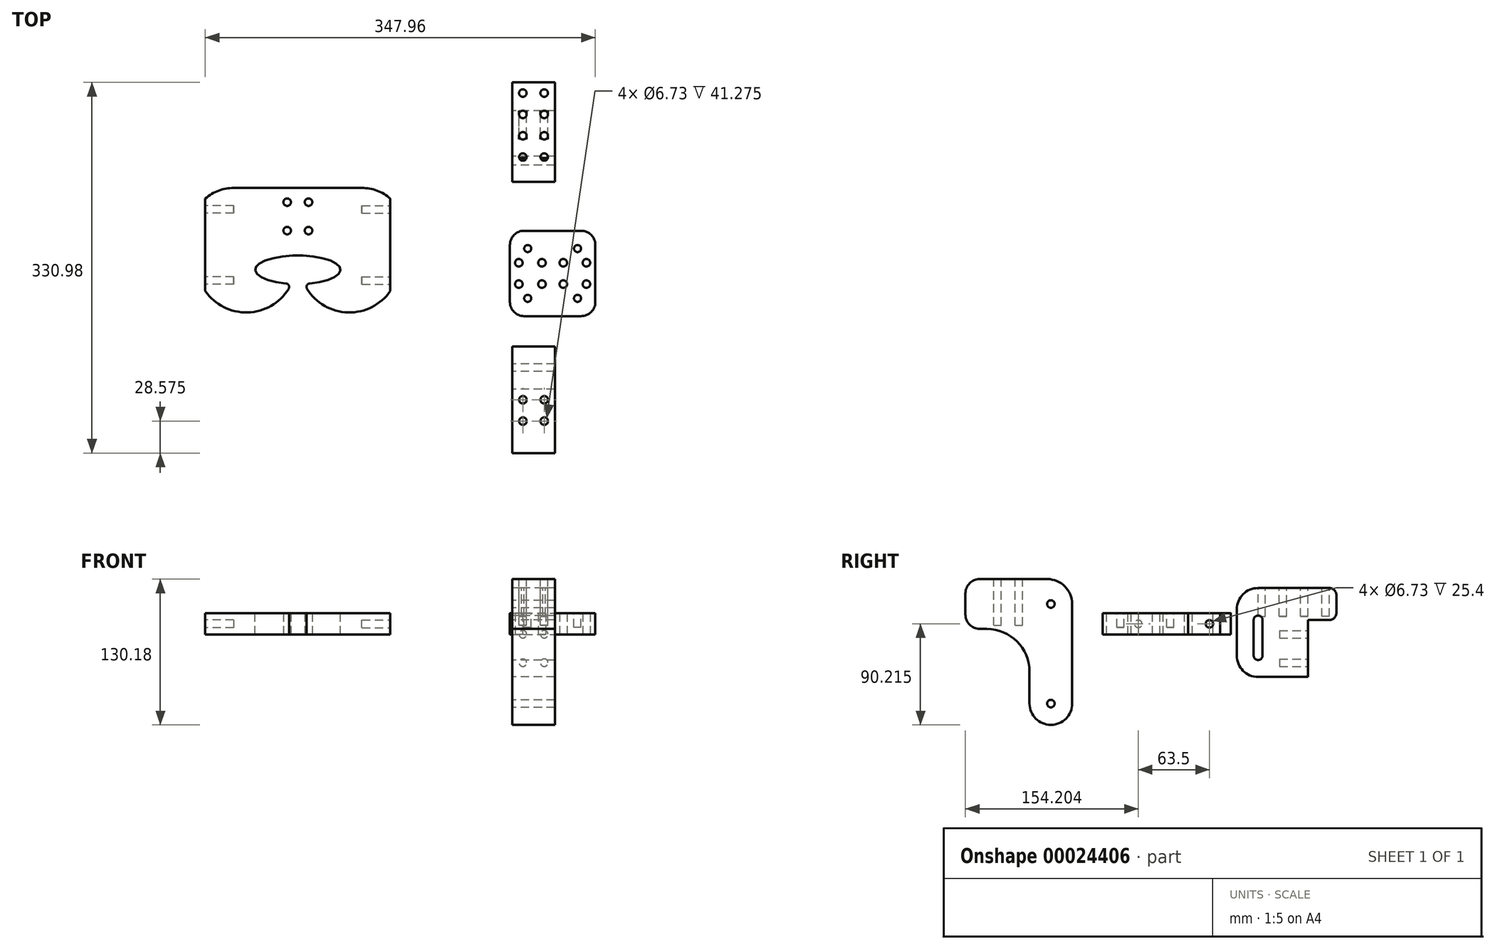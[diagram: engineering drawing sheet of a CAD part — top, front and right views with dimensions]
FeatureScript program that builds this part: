
annotation { "Feature Type Name" : "Feature", "Feature Type Description" : "" }
export const myFeature = defineFeature(function(context is Context, id is Id, definition is map)
    precondition{}
    {
        {
            var Q0;
            Q0=qCreatedBy(makeId("Top.planeOp"),FACE);
            var sketch = newSketch(context, id + "F0", { "sketchPlane" : qUnion([Q0])});
            skLineSegment(sketch, "E0.bottom", {"start": v(10.68, 0) * mm, "end": v(61.48, 0) * mm});
            skLineSegment(sketch, "E0.top", {"start": v(10.68, 76.2) * mm, "end": v(61.48, 76.2) * mm});
            skLineSegment(sketch, "E0.left", {"start": v(-2.02, 12.7) * mm, "end": v(-2.02, 63.5) * mm});
            skLineSegment(sketch, "E0.right", {"start": v(74.18, 12.7) * mm, "end": v(74.18, 63.5) * mm});
            skPoint(sketch, "E1.visualSharp", {"position": v(-2.02, 76.2) * mm});
            skArc(sketch, "E1.filletArc", {"start": v(10.68, 76.2) * mm, "mid": v(1.7, 72.48) * mm, "end": v(-2.02, 63.5) * mm});
            skPoint(sketch, "E2.visualSharp", {"position": v(74.18, 76.2) * mm});
            skArc(sketch, "E2.filletArc", {"start": v(74.18, 63.5) * mm, "mid": v(70.46, 72.48) * mm, "end": v(61.48, 76.2) * mm});
            skPoint(sketch, "E3.visualSharp", {"position": v(74.18, 0) * mm});
            skArc(sketch, "E3.filletArc", {"start": v(61.48, 0) * mm, "mid": v(70.46, 3.72) * mm, "end": v(74.18, 12.7) * mm});
            skPoint(sketch, "E4.visualSharp", {"position": v(-2.02, 0) * mm});
            skArc(sketch, "E4.filletArc", {"start": v(-2.02, 12.7) * mm, "mid": v(1.7, 3.72) * mm, "end": v(10.68, 0) * mm});
            skCircle(sketch, "E5", {"center": v(26.56, 28.57) * mm, "radius": 3.37 * mm});
            skCircle(sketch, "E6", {"center": v(26.56, 47.62) * mm, "radius": 3.37 * mm});
            skCircle(sketch, "E7", {"center": v(45.6, 47.62) * mm, "radius": 3.37 * mm});
            skCircle(sketch, "E8", {"center": v(45.6, 28.57) * mm, "radius": 3.37 * mm});
            skLineSegment(sketch, "E9", {"start": v(26.56, 47.62) * mm, "end": v(45.6, 47.62) * mm, "construction": true});
            skLineSegment(sketch, "E10", {"start": v(45.6, 28.58) * mm, "end": v(26.56, 28.58) * mm, "construction": true});
            skLineSegment(sketch, "E11", {"start": v(26.56, 47.62) * mm, "end": v(26.56, 28.57) * mm, "construction": true});
            skLineSegment(sketch, "E12", {"start": v(45.6, 47.62) * mm, "end": v(45.6, 28.57) * mm, "construction": true});
            skLineSegment(sketch, "E13", {"start": v(36.08, 28.58) * mm, "end": v(36.08, 0) * mm, "construction": true});
            skLineSegment(sketch, "E14", {"start": v(26.56, 38.1) * mm, "end": v(-2.02, 38.1) * mm, "construction": true});
            skLineSegment(sketch, "E15", {"start": v(45.6, 47.62) * mm, "end": v(74.18, 47.63) * mm, "construction": true});
            skLineSegment(sketch, "E16", {"start": v(26.56, 47.62) * mm, "end": v(-2.02, 47.62) * mm, "construction": true});
            skLineSegment(sketch, "E17", {"start": v(26.56, 28.57) * mm, "end": v(-2.02, 28.57) * mm, "construction": true});
            skLineSegment(sketch, "E18", {"start": v(45.6, 28.57) * mm, "end": v(74.18, 28.57) * mm, "construction": true});
            skCircle(sketch, "E19", {"center": v(66.23, 28.58) * mm, "radius": 3.37 * mm});
            skCircle(sketch, "E20", {"center": v(66.23, 47.63) * mm, "radius": 3.37 * mm});
            skCircle(sketch, "E21", {"center": v(5.93, 47.62) * mm, "radius": 3.37 * mm});
            skCircle(sketch, "E22", {"center": v(5.93, 28.57) * mm, "radius": 3.37 * mm});
            skSolve(sketch);
        }
        {
            var Q0;
            Q0 = qSketchRegion(id + "F0", true);
            extrude(context, id + "F1", {"entities" : qUnion([Q0]), "depth" : 19.05 * mm});
        }
        {
            var Q0;
            Q0=makeQuery(id+"F1.opExtrude","CAP_FACE",FACE,{"disambiguationData":[OSD([sQuery(id+"F0.wireOp",EDGE,"E0.bottom"),sQuery(id+"F0.wireOp",EDGE,"E0.top"),sQuery(id+"F0.wireOp",EDGE,"E0.left"),sQuery(id+"F0.wireOp",EDGE,"E0.right"),sQuery(id+"F0.wireOp",EDGE,"E1.filletArc"),sQuery(id+"F0.wireOp",EDGE,"E2.filletArc"),sQuery(id+"F0.wireOp",EDGE,"E3.filletArc"),sQuery(id+"F0.wireOp",EDGE,"E4.filletArc"),sQuery(id+"F0.wireOp",EDGE,"E5"),sQuery(id+"F0.wireOp",EDGE,"E6"),sQuery(id+"F0.wireOp",EDGE,"E7"),sQuery(id+"F0.wireOp",EDGE,"E8")])],"isStart":false});
            var sketch = newSketch(context, id + "F2", { "sketchPlane" : qUnion([Q0])});
            skCircle(sketch, "E23", {"center": v(13.86, 60.33) * mm, "radius": 3.18 * mm});
            skCircle(sketch, "E24", {"center": v(58.3, 60.33) * mm, "radius": 3.18 * mm});
            skCircle(sketch, "E25", {"center": v(58.3, 15.88) * mm, "radius": 3.18 * mm});
            skCircle(sketch, "E26", {"center": v(13.86, 15.88) * mm, "radius": 3.18 * mm});
            skLineSegment(sketch, "E27", {"start": v(13.86, 60.33) * mm, "end": v(58.3, 60.33) * mm, "construction": true});
            skLineSegment(sketch, "E28", {"start": v(58.3, 60.33) * mm, "end": v(58.3, 15.88) * mm, "construction": true});
            skLineSegment(sketch, "E29", {"start": v(58.3, 15.88) * mm, "end": v(13.86, 15.88) * mm, "construction": true});
            skLineSegment(sketch, "E30", {"start": v(13.86, 15.88) * mm, "end": v(13.86, 60.33) * mm, "construction": true});
            skLineSegment(sketch, "E31", {"start": v(36.08, 0) * mm, "end": v(36.08, 15.88) * mm, "construction": true});
            skLineSegment(sketch, "E32", {"start": v(13.86, 38.1) * mm, "end": v(-2.02, 38.1) * mm, "construction": true});
            skSolve(sketch);
        }
        {
            var Q0;
            Q0=makeQuery(id+"F2.imprint","IMPRINT",FACE,{"disambiguationData":[TD([[makeQuery(id+"F2.imprint","IMPRINT",EDGE,{"derivedFrom":sQuery(id+"F2.wireOp",EDGE,"E23")}),1.0]])]});
            var Q1;
            Q1=makeQuery(id+"F2.imprint","IMPRINT",FACE,{"disambiguationData":[TD([[makeQuery(id+"F2.imprint","IMPRINT",EDGE,{"derivedFrom":sQuery(id+"F2.wireOp",EDGE,"E24")}),1.0]])]});
            var Q2;
            Q2=makeQuery(id+"F2.imprint","IMPRINT",FACE,{"disambiguationData":[TD([[makeQuery(id+"F2.imprint","IMPRINT",EDGE,{"derivedFrom":sQuery(id+"F2.wireOp",EDGE,"E25")}),1.0]])]});
            var Q3;
            Q3=makeQuery(id+"F2.imprint","IMPRINT",FACE,{"disambiguationData":[TD([[makeQuery(id+"F2.imprint","IMPRINT",EDGE,{"derivedFrom":sQuery(id+"F2.wireOp",EDGE,"E26")}),1.0]])]});
            var Q4;
            Q4=sQuery(id+"F2.wireOp",EDGE,"E23");
            var Q5;
            Q5=sQuery(id+"F2.wireOp",EDGE,"E26");
            var Q6;
            Q6=sQuery(id+"F2.wireOp",EDGE,"E25");
            var Q7;
            Q7=sQuery(id+"F2.wireOp",EDGE,"E24");
            extrude(context, id + "F3", {"entities" : qUnion([Q0, Q1, Q2, Q3]), "operationType" : NewBodyOperationType.REMOVE, "surfaceEntities" : qUnion([Q4, Q5, Q6, Q7]), "oppositeDirection" : true, "depth" : 12.7 * mm});
        }
        {
            var Q0;
            Q0=qCreatedBy(makeId("Right.planeOp"),FACE);
            var sketch = newSketch(context, id + "F4", { "sketchPlane" : qUnion([Q0])});
            skLineSegment(sketch, "E33.bottom", {"start": v(-49.27, 49.49) * mm, "end": v(-109.6, 49.49) * mm});
            skLineSegment(sketch, "E33.top", {"start": v(-46.1, -80.69) * mm, "end": v(-46.1, -80.69) * mm});
            skLineSegment(sketch, "E33.left", {"start": v(-27.04, 27.26) * mm, "end": v(-27.04, -61.64) * mm});
            skLineSegment(sketch, "E33.right", {"start": v(-122.3, 36.79) * mm, "end": v(-122.3, 17.74) * mm});
            skLineSegment(sketch, "E34", {"start": v(-65.14, -61.64) * mm, "end": v(-65.14, -33.06) * mm});
            skLineSegment(sketch, "E35", {"start": v(-103.24, 5.04) * mm, "end": v(-109.6, 5.04) * mm});
            skPoint(sketch, "E36.visualSharp", {"position": v(-27.04, 49.49) * mm});
            skArc(sketch, "E36.filletArc", {"start": v(-27.04, 27.26) * mm, "mid": v(-33.55, 42.98) * mm, "end": v(-49.27, 49.49) * mm});
            skPoint(sketch, "E37.visualSharp", {"position": v(-122.3, 49.49) * mm});
            skArc(sketch, "E37.filletArc", {"start": v(-109.6, 49.49) * mm, "mid": v(-118.57, 45.77) * mm, "end": v(-122.3, 36.79) * mm});
            skPoint(sketch, "E38.visualSharp", {"position": v(-122.3, 5.04) * mm});
            skArc(sketch, "E38.filletArc", {"start": v(-122.3, 17.74) * mm, "mid": v(-118.57, 8.76) * mm, "end": v(-109.6, 5.04) * mm});
            skPoint(sketch, "E39.visualSharp", {"position": v(-65.14, -80.69) * mm});
            skArc(sketch, "E39.filletArc", {"start": v(-65.14, -61.64) * mm, "mid": v(-59.56, -75.1) * mm, "end": v(-46.1, -80.69) * mm});
            skPoint(sketch, "E40.visualSharp", {"position": v(-27.04, -80.69) * mm});
            skArc(sketch, "E40.filletArc", {"start": v(-46.1, -80.69) * mm, "mid": v(-32.62, -75.1) * mm, "end": v(-27.04, -61.64) * mm});
            skPoint(sketch, "E41.visualSharp", {"position": v(-65.14, 5.04) * mm});
            skArc(sketch, "E41.filletArc", {"start": v(-65.14, -33.06) * mm, "mid": v(-76.3, -6.12) * mm, "end": v(-103.24, 5.04) * mm});
            skCircle(sketch, "E42", {"center": v(-46.1, 27.26) * mm, "radius": 3.37 * mm});
            skCircle(sketch, "E43", {"center": v(-46.1, -61.64) * mm, "radius": 3.37 * mm});
            skSolve(sketch);
        }
        {
            var Q0;
            Q0=makeQuery(id+"F4.imprint","IMPRINT",FACE,{"disambiguationData":[TD([[makeQuery(id+"F4.imprint","IMPRINT",EDGE,{"derivedFrom":sQuery(id+"F4.wireOp",EDGE,"E33.bottom")}),1.0]])]});
            extrude(context, id + "F5", {"entities" : qUnion([Q0]), "depth" : 38.1 * mm});
        }
        {
            var Q0;
            Q0=makeQuery(id+"F5.opExtrude","SWEPT_FACE",FACE,{"disambiguationData":[OSD([sQuery(id+"F4.wireOp",EDGE,"E33.bottom")])]});
            var sketch = newSketch(context, id + "F6", { "sketchPlane" : qUnion([Q0])});
            skLineSegment(sketch, "E44", {"start": v(19.05, -49.27) * mm, "end": v(19.05, -109.6) * mm, "construction": true});
            skCircle(sketch, "E45", {"center": v(28.58, -93.72) * mm, "radius": 3.37 * mm});
            skCircle(sketch, "E46", {"center": v(28.58, -74.67) * mm, "radius": 3.37 * mm});
            skCircle(sketch, "E47", {"center": v(9.53, -74.67) * mm, "radius": 3.37 * mm});
            skCircle(sketch, "E48", {"center": v(9.53, -93.72) * mm, "radius": 3.37 * mm});
            skLineSegment(sketch, "E49", {"start": v(9.53, -74.67) * mm, "end": v(19.05, -74.67) * mm, "construction": true});
            skLineSegment(sketch, "E50", {"start": v(28.58, -93.72) * mm, "end": v(28.58, -74.67) * mm, "construction": true});
            skLineSegment(sketch, "E51", {"start": v(9.53, -93.72) * mm, "end": v(28.58, -93.72) * mm, "construction": true});
            skLineSegment(sketch, "E52", {"start": v(9.53, -93.72) * mm, "end": v(9.53, -74.67) * mm, "construction": true});
            skLineSegment(sketch, "E53", {"start": v(19.05, -74.67) * mm, "end": v(28.58, -74.67) * mm, "construction": true});
            skSolve(sketch);
        }
        {
            var Q0;
            Q0=makeQuery(id+"F6.imprint","IMPRINT",FACE,{"disambiguationData":[TD([[makeQuery(id+"F6.imprint","IMPRINT",EDGE,{"derivedFrom":sQuery(id+"F6.wireOp",EDGE,"E47")}),1.0]])]});
            var Q1;
            Q1=makeQuery(id+"F6.imprint","IMPRINT",FACE,{"disambiguationData":[TD([[makeQuery(id+"F6.imprint","IMPRINT",EDGE,{"derivedFrom":sQuery(id+"F6.wireOp",EDGE,"E46")}),1.0]])]});
            var Q2;
            Q2=makeQuery(id+"F6.imprint","IMPRINT",FACE,{"disambiguationData":[TD([[makeQuery(id+"F6.imprint","IMPRINT",EDGE,{"derivedFrom":sQuery(id+"F6.wireOp",EDGE,"E45")}),1.0]])]});
            var Q3;
            Q3=makeQuery(id+"F6.imprint","IMPRINT",FACE,{"disambiguationData":[TD([[makeQuery(id+"F6.imprint","IMPRINT",EDGE,{"derivedFrom":sQuery(id+"F6.wireOp",EDGE,"E48")}),1.0]])]});
            extrude(context, id + "F7", {"entities" : qUnion([Q0, Q1, Q2, Q3]), "operationType" : NewBodyOperationType.REMOVE, "oppositeDirection" : true, "depth" : 41.27 * mm});
        }
        {
            var Q0;
            Q0=qCreatedBy(makeId("Right.planeOp"),FACE);
            var sketch = newSketch(context, id + "F8", { "sketchPlane" : qUnion([Q0])});
            skLineSegment(sketch, "E54.bottom", {"start": v(138.84, -37.85) * mm, "end": v(183.29, -37.85) * mm});
            skLineSegment(sketch, "E54.top", {"start": v(138.84, 41.52) * mm, "end": v(202.34, 41.52) * mm});
            skLineSegment(sketch, "E54.left", {"start": v(119.79, -18.8) * mm, "end": v(119.79, 22.47) * mm});
            skLineSegment(sketch, "E54.right", {"start": v(208.69, -37.85) * mm, "end": v(208.69, 12.95) * mm, "construction": true});
            skLineSegment(sketch, "E55", {"start": v(183.29, -37.85) * mm, "end": v(183.29, -37.85) * mm});
            skLineSegment(sketch, "E56", {"start": v(183.29, 12.95) * mm, "end": v(202.34, 12.95) * mm});
            skLineSegment(sketch, "E57", {"start": v(183.29, -37.85) * mm, "end": v(183.29, 12.95) * mm});
            skLineSegment(sketch, "E58", {"start": v(208.69, 19.3) * mm, "end": v(208.69, 35.17) * mm});
            skLineSegment(sketch, "E59", {"start": v(183.29, -37.85) * mm, "end": v(208.69, -37.85) * mm, "construction": true});
            skPoint(sketch, "E60.visualSharp", {"position": v(119.79, 41.52) * mm});
            skArc(sketch, "E60.filletArc", {"start": v(138.84, 41.52) * mm, "mid": v(125.37, 35.94) * mm, "end": v(119.79, 22.47) * mm});
            skPoint(sketch, "E61.visualSharp", {"position": v(119.79, -37.85) * mm});
            skArc(sketch, "E61.filletArc", {"start": v(119.79, -18.8) * mm, "mid": v(125.37, -32.27) * mm, "end": v(138.84, -37.85) * mm});
            skPoint(sketch, "E62.visualSharp", {"position": v(208.69, 41.52) * mm});
            skArc(sketch, "E62.filletArc", {"start": v(208.69, 35.17) * mm, "mid": v(206.83, 39.66) * mm, "end": v(202.34, 41.52) * mm});
            skPoint(sketch, "E63.visualSharp", {"position": v(208.69, 12.95) * mm});
            skArc(sketch, "E63.filletArc", {"start": v(202.34, 12.95) * mm, "mid": v(206.83, 14.8) * mm, "end": v(208.69, 19.3) * mm});
            skArc(sketch, "E64", {"start": v(134.86, -18.8) * mm, "mid": v(138.84, -22.78) * mm, "end": v(142.81, -18.8) * mm});
            skArc(sketch, "E65", {"start": v(142.81, 12.95) * mm, "mid": v(138.84, 16.92) * mm, "end": v(134.86, 12.95) * mm});
            skLineSegment(sketch, "E66", {"start": v(142.81, 12.95) * mm, "end": v(142.81, -18.8) * mm});
            skLineSegment(sketch, "E67", {"start": v(134.86, 12.95) * mm, "end": v(134.86, -18.8) * mm});
            skSolve(sketch);
        }
        {
            var Q0;
            Q0 = qSketchRegion(id + "F8", true);
            extrude(context, id + "F9", {"entities" : qUnion([Q0]), "depth" : 38.1 * mm});
        }
        {
            var Q0;
            Q0=makeQuery(id+"F9.opExtrude","SWEPT_FACE",FACE,{"disambiguationData":[OSD([sQuery(id+"F8.wireOp",EDGE,"E54.top")])]});
            var sketch = newSketch(context, id + "F10", { "sketchPlane" : qUnion([Q0])});
            skCircle(sketch, "E68", {"center": v(28.58, 199.16) * mm, "radius": 3.37 * mm});
            skCircle(sketch, "E69", {"center": v(28.58, 180.11) * mm, "radius": 3.37 * mm});
            skCircle(sketch, "E70", {"center": v(28.58, 161.06) * mm, "radius": 3.37 * mm});
            skCircle(sketch, "E71", {"center": v(28.58, 142.01) * mm, "radius": 3.37 * mm});
            skCircle(sketch, "E72", {"center": v(9.53, 142.01) * mm, "radius": 3.37 * mm});
            skCircle(sketch, "E73", {"center": v(9.53, 161.06) * mm, "radius": 3.37 * mm});
            skCircle(sketch, "E74", {"center": v(9.53, 180.11) * mm, "radius": 3.37 * mm});
            skCircle(sketch, "E75", {"center": v(9.53, 199.16) * mm, "radius": 3.37 * mm});
            skSolve(sketch);
        }
        {
            var Q0;
            {var subQ0=makeQuery(id+"F9.opExtrude","SWEPT_EDGE",EDGE,{"disambiguationData":[OSD([sQuery(id+"F8.wireOp",EDGE,"E54.top"),sQuery(id+"F8.wireOp",EDGE,"E62.filletArc")])]});var subQ1=sQuery(id+"F10.wireOp",EDGE,"E75");var subQ3=makeQuery(id+"F10.imprint","INTERSECT",VERTEX,{"disambiguationData":[OD(0.0)],"derivedFrom":[subQ0,subQ1]});Q0=makeQuery(id+"F10.imprint","IMPRINT",FACE,{"disambiguationData":[TD([[makeQuery(id+"F10.imprint","IMPRINT",EDGE,{"disambiguationData":[TD([[subQ3,-1.0]])],"derivedFrom":subQ1}),1.0]])]});}
            var Q1;
            Q1=makeQuery(id+"F10.imprint","IMPRINT",FACE,{"disambiguationData":[TD([[makeQuery(id+"F10.imprint","IMPRINT",EDGE,{"derivedFrom":sQuery(id+"F10.wireOp",EDGE,"E69")}),1.0]])]});
            var Q2;
            Q2=makeQuery(id+"F10.imprint","IMPRINT",FACE,{"disambiguationData":[TD([[makeQuery(id+"F10.imprint","IMPRINT",EDGE,{"derivedFrom":sQuery(id+"F10.wireOp",EDGE,"E74")}),1.0]])]});
            var Q3;
            Q3=makeQuery(id+"F10.imprint","IMPRINT",FACE,{"disambiguationData":[TD([[makeQuery(id+"F10.imprint","IMPRINT",EDGE,{"derivedFrom":sQuery(id+"F10.wireOp",EDGE,"E70")}),1.0]])]});
            var Q4;
            {var subQ0=makeQuery(id+"F9.opExtrude","SWEPT_EDGE",EDGE,{"disambiguationData":[OSD([sQuery(id+"F8.wireOp",EDGE,"E54.top"),sQuery(id+"F8.wireOp",EDGE,"E60.filletArc")])]});var subQ1=sQuery(id+"F10.wireOp",EDGE,"E71");var subQ3=makeQuery(id+"F10.imprint","INTERSECT",VERTEX,{"disambiguationData":[OD(0.0)],"derivedFrom":[subQ0,subQ1]});Q4=makeQuery(id+"F10.imprint","IMPRINT",FACE,{"disambiguationData":[TD([[makeQuery(id+"F10.imprint","IMPRINT",EDGE,{"disambiguationData":[TD([[subQ3,-1.0]])],"derivedFrom":subQ1}),1.0]])]});}
            var Q5;
            {var subQ0=makeQuery(id+"F9.opExtrude","SWEPT_EDGE",EDGE,{"disambiguationData":[OSD([sQuery(id+"F8.wireOp",EDGE,"E54.top"),sQuery(id+"F8.wireOp",EDGE,"E60.filletArc")])]});var subQ1=sQuery(id+"F10.wireOp",EDGE,"E72");var subQ3=makeQuery(id+"F10.imprint","INTERSECT",VERTEX,{"disambiguationData":[OD(0.0)],"derivedFrom":[subQ0,subQ1]});Q5=makeQuery(id+"F10.imprint","IMPRINT",FACE,{"disambiguationData":[TD([[makeQuery(id+"F10.imprint","IMPRINT",EDGE,{"disambiguationData":[TD([[subQ3,1.0]])],"derivedFrom":subQ1}),1.0]])]});}
            var Q6;
            Q6=makeQuery(id+"F10.imprint","IMPRINT",FACE,{"disambiguationData":[TD([[makeQuery(id+"F10.imprint","IMPRINT",EDGE,{"derivedFrom":sQuery(id+"F10.wireOp",EDGE,"E73")}),1.0]])]});
            var Q7;
            {var subQ0=makeQuery(id+"F9.opExtrude","SWEPT_EDGE",EDGE,{"disambiguationData":[OSD([sQuery(id+"F8.wireOp",EDGE,"E54.top"),sQuery(id+"F8.wireOp",EDGE,"E62.filletArc")])]});var subQ1=sQuery(id+"F10.wireOp",EDGE,"E68");var subQ3=makeQuery(id+"F10.imprint","INTERSECT",VERTEX,{"disambiguationData":[OD(0.0)],"derivedFrom":[subQ0,subQ1]});Q7=makeQuery(id+"F10.imprint","IMPRINT",FACE,{"disambiguationData":[TD([[makeQuery(id+"F10.imprint","IMPRINT",EDGE,{"disambiguationData":[TD([[subQ3,1.0]])],"derivedFrom":subQ1}),1.0]])]});}
            extrude(context, id + "F11", {"entities" : qUnion([Q0, Q1, Q2, Q3, Q4, Q5, Q6, Q7]), "operationType" : NewBodyOperationType.REMOVE, "oppositeDirection" : true, "depth" : 25.4 * mm});
        }
        {
            var Q0;
            Q0=makeQuery(id+"F9.opExtrude","SWEPT_FACE",FACE,{"disambiguationData":[OSD([sQuery(id+"F8.wireOp",EDGE,"E57")])]});
            var sketch = newSketch(context, id + "F12", { "sketchPlane" : qUnion([Q0])});
            skCircle(sketch, "E76", {"center": v(-9.53, 0.25) * mm, "radius": 3.37 * mm});
            skCircle(sketch, "E77", {"center": v(-9.52, -25.15) * mm, "radius": 3.37 * mm});
            skCircle(sketch, "E78", {"center": v(-28.57, -25.15) * mm, "radius": 3.37 * mm});
            skCircle(sketch, "E79", {"center": v(-28.58, 0.25) * mm, "radius": 3.37 * mm});
            skSolve(sketch);
        }
        {
            var Q0;
            Q0=makeQuery(id+"F12.imprint","IMPRINT",FACE,{"disambiguationData":[TD([[makeQuery(id+"F12.imprint","IMPRINT",EDGE,{"derivedFrom":sQuery(id+"F12.wireOp",EDGE,"E76")}),1.0]])]});
            var Q1;
            Q1=makeQuery(id+"F12.imprint","IMPRINT",FACE,{"disambiguationData":[TD([[makeQuery(id+"F12.imprint","IMPRINT",EDGE,{"derivedFrom":sQuery(id+"F12.wireOp",EDGE,"E77")}),1.0]])]});
            var Q2;
            Q2=makeQuery(id+"F12.imprint","IMPRINT",FACE,{"disambiguationData":[TD([[makeQuery(id+"F12.imprint","IMPRINT",EDGE,{"derivedFrom":sQuery(id+"F12.wireOp",EDGE,"E78")}),1.0]])]});
            var Q3;
            Q3=makeQuery(id+"F12.imprint","IMPRINT",FACE,{"disambiguationData":[TD([[makeQuery(id+"F12.imprint","IMPRINT",EDGE,{"derivedFrom":sQuery(id+"F12.wireOp",EDGE,"E79")}),1.0]])]});
            extrude(context, id + "F13", {"entities" : qUnion([Q0, Q1, Q2, Q3]), "operationType" : NewBodyOperationType.REMOVE, "oppositeDirection" : true, "depth" : 25.4 * mm});
        }
        {
            var Q0;
            Q0=qCreatedBy(makeId("Top.planeOp"),FACE);
            var sketch = newSketch(context, id + "F14", { "sketchPlane" : qUnion([Q0])});
            skLineSegment(sketch, "E80.bottom", {"start": v(-108.68, 3.34) * mm, "end": v(-273.78, 3.34) * mm, "construction": true});
            skLineSegment(sketch, "E80.top", {"start": v(-108.68, 114.46) * mm, "end": v(-134.08, 114.46) * mm, "construction": true});
            skLineSegment(sketch, "E80.left", {"start": v(-108.68, 3.34) * mm, "end": v(-108.68, 22.39) * mm, "construction": true});
            skLineSegment(sketch, "E80.right", {"start": v(-273.78, 3.34) * mm, "end": v(-273.78, 22.39) * mm, "construction": true});
            skCircle(sketch, "E81", {"center": v(-200.75, 101.76) * mm, "radius": 3.37 * mm});
            skCircle(sketch, "E82", {"center": v(-200.75, 76.36) * mm, "radius": 3.37 * mm});
            skCircle(sketch, "E83", {"center": v(-181.7, 76.36) * mm, "radius": 3.37 * mm});
            skCircle(sketch, "E84", {"center": v(-181.7, 101.76) * mm, "radius": 3.37 * mm});
            skLineSegment(sketch, "E85", {"start": v(-191.23, 3.34) * mm, "end": v(-191.23, 114.46) * mm, "construction": true});
            skEllipticalArc(sketch, "E86", {});
            skLineSegment(sketch, "E87", {"start": v(-273.78, 22.39) * mm, "end": v(-108.68, 22.39) * mm, "construction": true});
            skLineSegment(sketch, "E88", {"start": v(-235.68, 22.39) * mm, "end": v(-235.68, 3.34) * mm, "construction": true});
            skLineSegment(sketch, "E89", {"start": v(-146.78, 22.39) * mm, "end": v(-146.78, 3.34) * mm, "construction": true});
            skArc(sketch, "E90", {"start": v(-183, 24.41) * mm, "mid": v(-146.39, 3.33) * mm, "end": v(-108.68, 22.39) * mm});
            skArc(sketch, "E91", {"start": v(-273.78, 22.39) * mm, "mid": v(-236.07, 3.33) * mm, "end": v(-199.45, 24.41) * mm});
            skLineSegment(sketch, "E92", {"start": v(-108.68, 22.39) * mm, "end": v(-108.68, 104.94) * mm});
            skLineSegment(sketch, "E93", {"start": v(-273.78, 22.39) * mm, "end": v(-273.78, 104.94) * mm});
            skArc(sketch, "E94", {"start": v(-180.6, 29.24) * mm, "mid": v(-183.14, 27.5) * mm, "end": v(-183, 24.41) * mm});
            skArc(sketch, "E95", {"start": v(-199.45, 24.41) * mm, "mid": v(-199.31, 27.5) * mm, "end": v(-201.85, 29.24) * mm});
            skArc(sketch, "E96", {"start": v(-108.68, 104.94) * mm, "mid": v(-120.5, 112.04) * mm, "end": v(-134.08, 114.46) * mm});
            skLineSegment(sketch, "E97", {"start": v(-134.08, 114.46) * mm, "end": v(-248.38, 114.46) * mm});
            skLineSegment(sketch, "E98", {"start": v(-108.68, 104.94) * mm, "end": v(-108.68, 114.46) * mm, "construction": true});
            skLineSegment(sketch, "E99", {"start": v(-273.78, 104.94) * mm, "end": v(-273.78, 114.46) * mm, "construction": true});
            skLineSegment(sketch, "E100", {"start": v(-248.38, 114.46) * mm, "end": v(-273.78, 114.46) * mm, "construction": true});
            skArc(sketch, "E101.trimOffspring", {"start": v(-248.38, 114.46) * mm, "mid": v(-261.96, 112.04) * mm, "end": v(-273.78, 104.94) * mm});
            const initialGuessF14  = {"E86": [-0.1912288818459131, 0.04143897414000486, -1, 0, 0.0381, 0.0127, 1.8533354671619715, 1.288257186427824]};
            skSetInitialGuess(sketch, initialGuessF14);
            skSolve(sketch);
        }
        {
            var Q0;
            Q0=makeQuery(id+"F14.imprint","IMPRINT",FACE,{"disambiguationData":[TD([[makeQuery(id+"F14.imprint","IMPRINT",EDGE,{"derivedFrom":sQuery(id+"F14.wireOp",EDGE,"E81")}),-1.0]])]});
            extrude(context, id + "F15", {"entities" : qUnion([Q0]), "depth" : 19.05 * mm});
        }
        {
            var Q0;
            Q0=makeQuery(id+"F15.opExtrude","SWEPT_FACE",FACE,{"disambiguationData":[OSD([sQuery(id+"F14.wireOp",EDGE,"E93")])]});
            var sketch = newSketch(context, id + "F16", { "sketchPlane" : qUnion([Q0])});
            skCircle(sketch, "E102", {"center": v(-95.41, 9.52) * mm, "radius": 3.37 * mm});
            skCircle(sketch, "E103", {"center": v(-31.91, 9.53) * mm, "radius": 3.37 * mm});
            skLineSegment(sketch, "E104", {"start": v(-104.94, 9.53) * mm, "end": v(-22.39, 9.53) * mm, "construction": true});
            skSolve(sketch);
        }
        {
            var Q0;
            Q0=makeQuery(id+"F16.imprint","IMPRINT",FACE,{"disambiguationData":[TD([[makeQuery(id+"F16.imprint","IMPRINT",EDGE,{"derivedFrom":sQuery(id+"F16.wireOp",EDGE,"E102")}),1.0]])]});
            var Q1;
            Q1=makeQuery(id+"F16.imprint","IMPRINT",FACE,{"disambiguationData":[TD([[makeQuery(id+"F16.imprint","IMPRINT",EDGE,{"derivedFrom":sQuery(id+"F16.wireOp",EDGE,"E103")}),1.0]])]});
            extrude(context, id + "F17", {"entities" : qUnion([Q0, Q1]), "operationType" : NewBodyOperationType.REMOVE, "oppositeDirection" : true, "depth" : 25.4 * mm});
        }
        {
            var Q0;
            Q0=makeQuery(id+"F15.opExtrude","SWEPT_FACE",FACE,{"disambiguationData":[OSD([sQuery(id+"F14.wireOp",EDGE,"E92")])]});
            var sketch = newSketch(context, id + "F18", { "sketchPlane" : qUnion([Q0])});
            skCircle(sketch, "E105", {"center": v(95.41, 9.53) * mm, "radius": 3.37 * mm});
            skCircle(sketch, "E106", {"center": v(31.91, 9.53) * mm, "radius": 3.37 * mm});
            skLineSegment(sketch, "E107", {"start": v(22.39, 9.53) * mm, "end": v(104.94, 9.53) * mm, "construction": true});
            skSolve(sketch);
        }
        {
            var Q0;
            Q0=makeQuery(id+"F18.imprint","IMPRINT",FACE,{"disambiguationData":[TD([[makeQuery(id+"F18.imprint","IMPRINT",EDGE,{"derivedFrom":sQuery(id+"F18.wireOp",EDGE,"E105")}),1.0]])]});
            var Q1;
            Q1=makeQuery(id+"F18.imprint","IMPRINT",FACE,{"disambiguationData":[TD([[makeQuery(id+"F18.imprint","IMPRINT",EDGE,{"derivedFrom":sQuery(id+"F18.wireOp",EDGE,"E106")}),1.0]])]});
            extrude(context, id + "F19", {"entities" : qUnion([Q0, Q1]), "operationType" : NewBodyOperationType.REMOVE, "oppositeDirection" : true, "depth" : 25.4 * mm});
        }
    });
